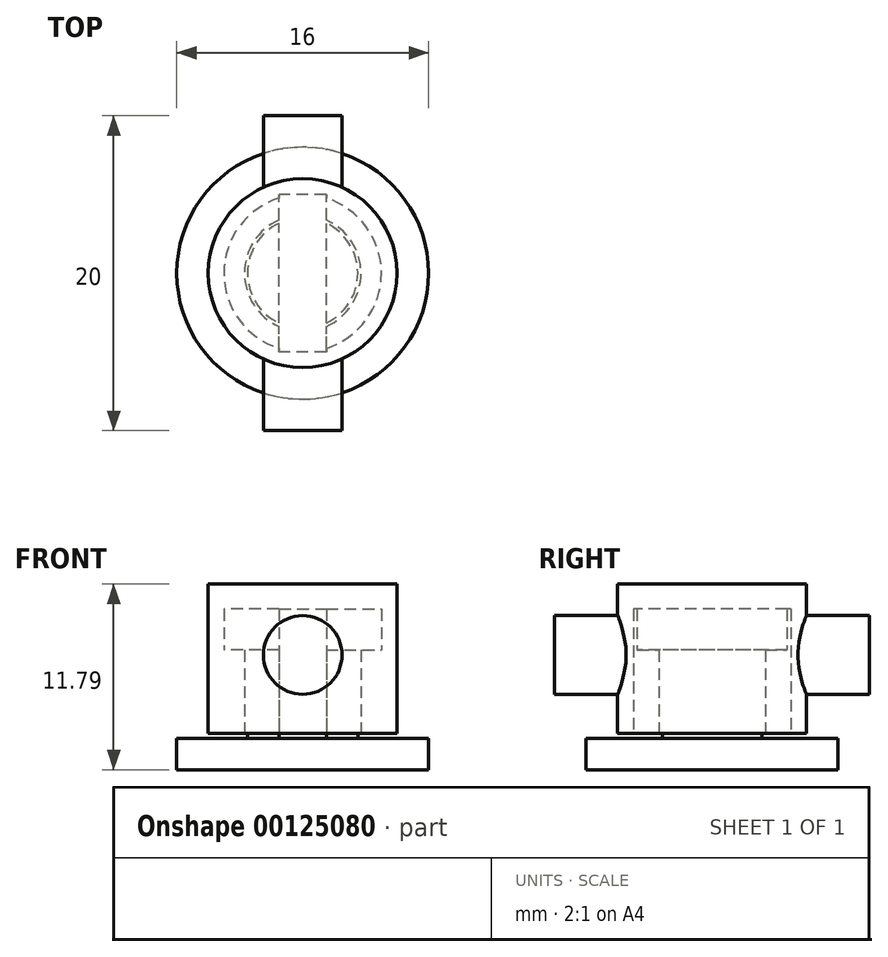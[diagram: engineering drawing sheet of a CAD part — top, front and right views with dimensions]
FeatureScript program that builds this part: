
annotation { "Feature Type Name" : "Feature", "Feature Type Description" : "" }
export const myFeature = defineFeature(function(context is Context, id is Id, definition is map)
    precondition{}
    {
        {
            var Q0;
            Q0=qCreatedBy(makeId("Front.planeOp"),FACE);
            var sketch = newSketch(context, id + "F0", { "sketchPlane" : qUnion([Q0])});
            skLineSegment(sketch, "E0", {"start": v(0, 8) * mm, "end": v(-3.5, 8) * mm});
            skLineSegment(sketch, "E1", {"start": v(-3.5, 8) * mm, "end": v(-3.5, 0) * mm});
            skLineSegment(sketch, "E2", {"start": v(0, 0) * mm, "end": v(0, 8) * mm});
            skLineSegment(sketch, "E3", {"start": v(-3.5, 0) * mm, "end": v(-8, 0) * mm});
            skLineSegment(sketch, "E4", {"start": v(-8, 0) * mm, "end": v(-8, -2) * mm});
            skLineSegment(sketch, "E5", {"start": v(-8, -2) * mm, "end": v(0, -2) * mm});
            skLineSegment(sketch, "E6", {"start": v(0, -2) * mm, "end": v(0, 0) * mm});
            skSolve(sketch);
        }
        {
            var Q0;
            Q0 = qSketchRegion(id + "F0", true);
            var Q1;
            Q1=sQuery(id+"F0.wireOp",EDGE,"E2");
            revolve(context, id + "F1", {"entities" : qUnion([Q0]), "axis" : qUnion([Q1]), "revolveType" : RevolveType.FULL});
        }
        {
            var Q0;
            Q0=qCreatedBy(makeId("Front.planeOp"),FACE);
            var sketch = newSketch(context, id + "F2", { "sketchPlane" : qUnion([Q0])});
            skCircle(sketch, "E7", {"center": v(0, 7) * mm, "radius": 1 * mm});
            skSolve(sketch);
        }
        {
            var Q0;
            Q0 = qSketchRegion(id + "F2", true);
            extrude(context, id + "F3", {"entities" : qUnion([Q0]), "operationType" : NewBodyOperationType.ADD, "endBound" : BoundingType.SYMMETRIC, "depth" : 8 * mm});
        }
        {
            var Q0;
            Q0=makeQuery(id+"F3.opExtrude","CAP_EDGE",EDGE,{"disambiguationData":[OSD([sQuery(id+"F2.wireOp",EDGE,"E7")])],"isStart":false});
            var Q1;
            Q1=makeQuery(id+"F3.opExtrude","CAP_EDGE",EDGE,{"disambiguationData":[OSD([sQuery(id+"F2.wireOp",EDGE,"E7")])],"isStart":true});
            fillet(context, id + "F4", {"entities" : qUnion([Q0, Q1]), "radius" : 0.5 * mm, "tangentPropagation" : true, "allowEdgeOverflow" : false});
        }
        {
            var Q0;
            Q0=qCreatedBy(makeId("Front.planeOp"),FACE);
            var sketch = newSketch(context, id + "F5", { "sketchPlane" : qUnion([Q0])});
            skLineSegment(sketch, "E8.0", {"start": v(-3.7, 8.2) * mm, "end": v(-3.7, 0.3) * mm});
            skLineSegment(sketch, "E8.2", {"start": v(0, 8.2) * mm, "end": v(-3.7, 8.2) * mm});
            skLineSegment(sketch, "E9", {"start": v(0, 8.2) * mm, "end": v(0, 9.8) * mm});
            skLineSegment(sketch, "E10", {"start": v(0, 9.8) * mm, "end": v(-6, 9.8) * mm});
            skLineSegment(sketch, "E11", {"start": v(-6, 9.8) * mm, "end": v(-6, 0.3) * mm});
            skLineSegment(sketch, "E12", {"start": v(-3.7, 0.3) * mm, "end": v(-6, 0.3) * mm});
            skPoint(sketch, "E13.orphan", {"position": v(-6, 0) * mm});
            skSolve(sketch);
        }
        {
            var Q0;
            Q0 = qSketchRegion(id + "F5", true);
            var Q1;
            Q1=sQuery(id+"F5.wireOp",EDGE,"E9");
            revolve(context, id + "F6", {"entities" : qUnion([Q0]), "axis" : qUnion([Q1]), "revolveType" : RevolveType.FULL});
        }
        {
            var Q0;
            Q0=qCreatedBy(makeId("Front.planeOp"),FACE);
            var sketch = newSketch(context, id + "F7", { "sketchPlane" : qUnion([Q0])});
            skCircle(sketch, "E14", {"center": v(0, 5.3) * mm, "radius": 2.5 * mm});
            skSolve(sketch);
        }
        {
            var Q0;
            Q0 = qSketchRegion(id + "F7", true);
            extrude(context, id + "F8", {"entities" : qUnion([Q0]), "operationType" : NewBodyOperationType.ADD, "endBound" : BoundingType.SYMMETRIC, "depth" : 20 * mm});
        }
        {
            var Q0;
            Q0=qCreatedBy(makeId("Front.planeOp"),FACE);
            var sketch = newSketch(context, id + "F9", { "sketchPlane" : qUnion([Q0])});
            skLineSegment(sketch, "E15.0", {"start": v(0, 8.2) * mm, "end": v(-3.7, 8.2) * mm});
            skLineSegment(sketch, "E15.2", {"start": v(-3.7, 5.6) * mm, "end": v(-3.7, 0.3) * mm});
            skLineSegment(sketch, "E16", {"start": v(0, 8.2) * mm, "end": v(0, 0.3) * mm});
            skLineSegment(sketch, "E17", {"start": v(0, 0.3) * mm, "end": v(-3.7, 0.3) * mm});
            skLineSegment(sketch, "E18.bottom", {"start": v(-3.7, 8.2) * mm, "end": v(-5, 8.2) * mm});
            skLineSegment(sketch, "E18.top", {"start": v(-3.7, 5.6) * mm, "end": v(-5, 5.6) * mm});
            skLineSegment(sketch, "E18.right", {"start": v(-5, 8.2) * mm, "end": v(-5, 5.6) * mm});
            skPoint(sketch, "E19.orphan", {"position": v(-3.7, 8.2) * mm});
            skSolve(sketch);
        }
        {
            var Q0;
            Q0 = qSketchRegion(id + "F9", true);
            var Q1;
            Q1=sQuery(id+"F9.wireOp",EDGE,"E16");
            revolve(context, id + "F10", {"operationType" : NewBodyOperationType.REMOVE, "entities" : qUnion([Q0]), "axis" : qUnion([Q1]), "revolveType" : RevolveType.FULL, "oppositeDirection" : true});
        }
        {
            var Q0;
            Q0=qCreatedBy(makeId("Top.planeOp"),FACE);
            var sketch = newSketch(context, id + "F11", { "sketchPlane" : qUnion([Q0])});
            skLineSegment(sketch, "E20.bottom", {"start": v(1.5, -5) * mm, "end": v(-1.5, -5) * mm});
            skLineSegment(sketch, "E20.top", {"start": v(1.5, 5) * mm, "end": v(-1.5, 5) * mm});
            skLineSegment(sketch, "E20.left", {"start": v(1.5, -5) * mm, "end": v(1.5, 5) * mm});
            skLineSegment(sketch, "E20.right", {"start": v(-1.5, -5) * mm, "end": v(-1.5, 5) * mm});
            skPoint(sketch, "E20.middle", {"position": v(0, 0) * mm});
            skSolve(sketch);
        }
        {
            var Q0;
            Q0 = qSketchRegion(id + "F11", true);
            var Q1;
            Q1=makeQuery(id+"F10.boolean.opBoolean","MERGE",FACE,{"derivedFrom":[makeQuery(id+"F6.opRevolve","SWEPT_FACE",FACE,{"disambiguationData":[OSD([sQuery(id+"F5.wireOp",EDGE,"E8.2")])]}),makeQuery(id+"F10.opRevolve","SWEPT_FACE",FACE,{"disambiguationData":[OSD([sQuery(id+"F9.wireOp",EDGE,"E15.0"),sQuery(id+"F9.wireOp",EDGE,"E18.bottom")])]})]});
            extrude(context, id + "F12", {"entities" : qUnion([Q0]), "operationType" : NewBodyOperationType.REMOVE, "endBound" : BoundingType.UP_TO_SURFACE, "endBoundEntityFace" : qUnion([Q1]), "depth" : 25 * mm});
        }
    });
